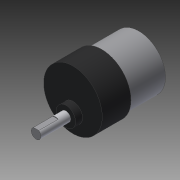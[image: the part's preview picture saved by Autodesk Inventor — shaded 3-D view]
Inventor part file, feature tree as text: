
AUTODESK INVENTOR PART (.ipt)
format: ipt  version: 2014 SP1 (Build 180222100, 222)  size: 135,168 bytes
history: native  units: in
note: dims shown in document units (in); Inventor stores cm internally (conversion verified against a paired STEP export)
features: sketch x7, other x3
ambient origin geometry x8: Origin, YZ Plane, XZ Plane, XY Plane, X Axis, Y Axis, Z Axis, Center Point
bodies: Solid1 (feature_tree)
feature tree (10):
  other  "Drive Motor.ipt"
  other  "Solid1::Drive Motor.ipt"
  other  "TaggingFeature1"
  sketch  "Sketch1"  dims[d0=0.3937in]
  sketch  "Sketch2"  dims[d1=0.7in d2=0.0in d3=0.449in d4=0.47in d5=0.17in d6=0.0in d7=0.2362in d8=0.725in d9=0.0in d11=0.4724in d12=0.0in d13=1.3in d14=0.9in d15=0.0in d16=0.35in d17=0.125in d18=0.0in d21=0.1181in d22=0.1181in d23=2.114in d24=2.114in d25=0.1181in d26=0.1181in d27=0.5in d28=0.0in]
  sketch  "Sketch3"
  sketch  "Sketch4"
  sketch  "Sketch5"
  sketch  "Sketch6"
  sketch  "Sketch7"
